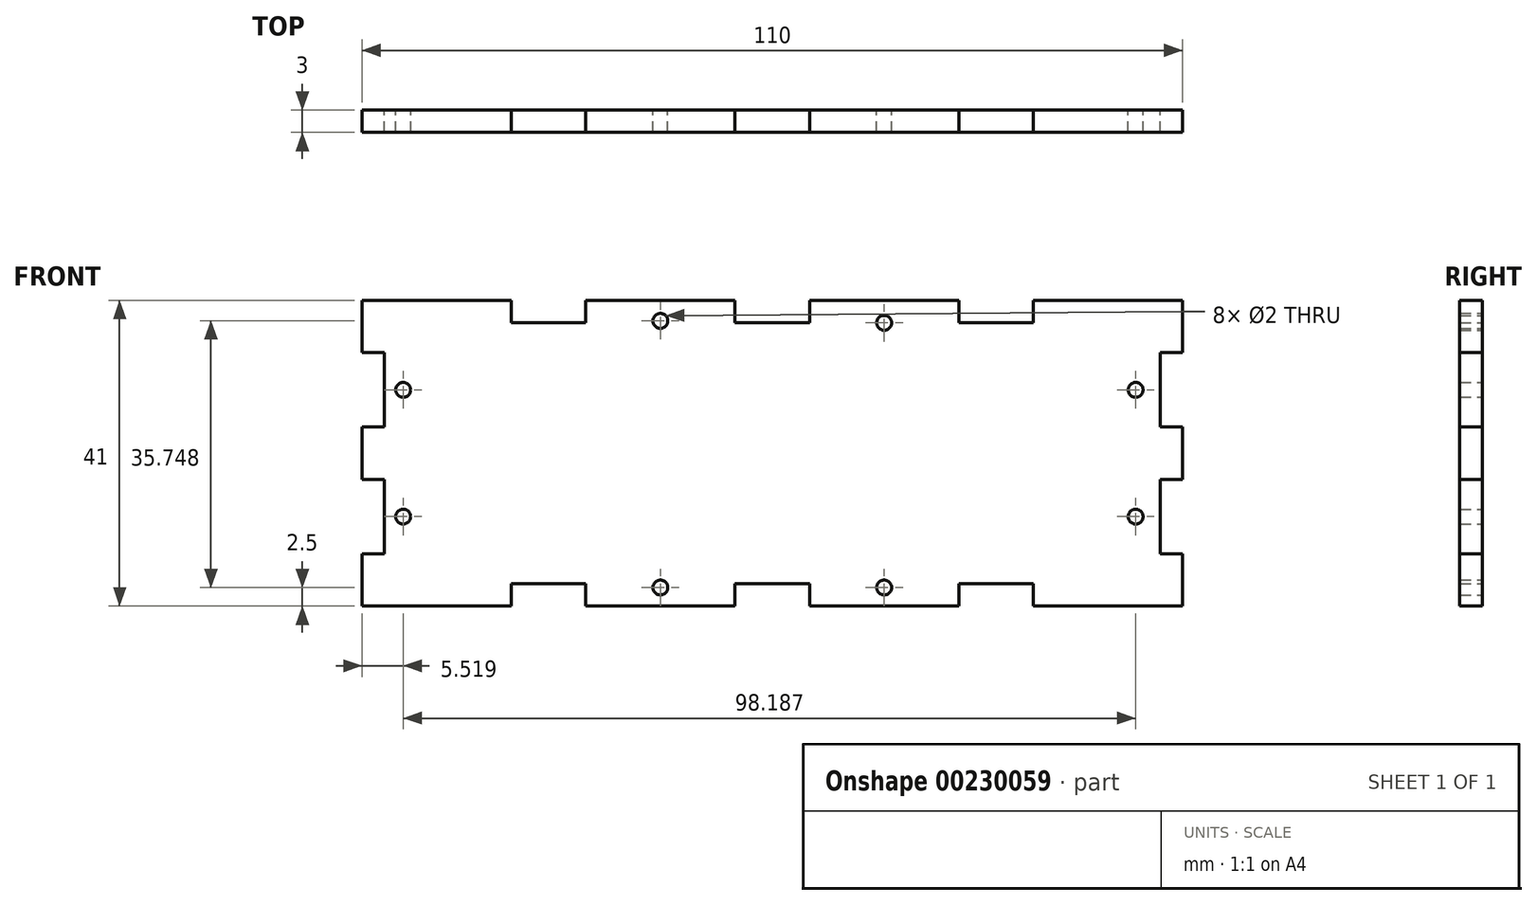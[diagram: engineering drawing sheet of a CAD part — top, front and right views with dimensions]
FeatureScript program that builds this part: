
annotation { "Feature Type Name" : "Feature", "Feature Type Description" : "" }
export const myFeature = defineFeature(function(context is Context, id is Id, definition is map)
    precondition{}
    {
        {
            var Q0;
            Q0=qCreatedBy(makeId("Front.planeOp"),FACE);
            var sketch = newSketch(context, id + "F0", { "sketchPlane" : qUnion([Q0])});
            skLineSegment(sketch, "E0", {"start": v(-54.97, 1.92) * mm, "end": v(-51.97, 1.92) * mm});
            skLineSegment(sketch, "E1", {"start": v(-51.97, 1.92) * mm, "end": v(-51.97, 11.92) * mm});
            skLineSegment(sketch, "E2", {"start": v(-51.97, 11.92) * mm, "end": v(-54.97, 11.92) * mm});
            skLineSegment(sketch, "E3", {"start": v(-54.97, 11.92) * mm, "end": v(-54.97, 18.92) * mm});
            skLineSegment(sketch, "E4", {"start": v(-54.97, 18.92) * mm, "end": v(-34.97, 18.92) * mm});
            skLineSegment(sketch, "E5", {"start": v(-34.97, 18.92) * mm, "end": v(-34.97, 15.92) * mm});
            skLineSegment(sketch, "E6", {"start": v(-34.97, 15.92) * mm, "end": v(-24.97, 15.92) * mm});
            skLineSegment(sketch, "E7", {"start": v(-24.97, 15.92) * mm, "end": v(-24.97, 18.92) * mm});
            skLineSegment(sketch, "E8", {"start": v(-4.97, 18.92) * mm, "end": v(-24.97, 18.92) * mm});
            skLineSegment(sketch, "E9", {"start": v(-4.97, 18.92) * mm, "end": v(-4.97, 15.92) * mm});
            skLineSegment(sketch, "E10", {"start": v(0.03, 15.92) * mm, "end": v(-4.97, 15.92) * mm});
            skCircle(sketch, "E11", {"center": v(-14.97, 16.17) * mm, "radius": 1 * mm});
            skCircle(sketch, "E12", {"center": v(-49.45, 6.92) * mm, "radius": 1 * mm});
            skCircle(sketch, "E13.MirrorC", {"center": v(15.03, 15.9) * mm, "radius": 1 * mm});
            skLineSegment(sketch, "E14", {"start": v(-54.97, 1.92) * mm, "end": v(-54.97, -1.58) * mm});
            skLineSegment(sketch, "E15.MirrorCS", {"start": v(52.03, 11.92) * mm, "end": v(55.03, 11.92) * mm});
            skLineSegment(sketch, "E16.MirrorCS", {"start": v(5.03, 18.92) * mm, "end": v(5.03, 15.92) * mm});
            skLineSegment(sketch, "E17.MirrorCS", {"start": v(35.03, 18.92) * mm, "end": v(35.03, 15.92) * mm});
            skLineSegment(sketch, "E18.MirrorCS", {"start": v(55.03, 1.92) * mm, "end": v(52.03, 1.92) * mm});
            skLineSegment(sketch, "E19.MirrorCS", {"start": v(25.03, 15.92) * mm, "end": v(25.03, 18.92) * mm});
            skCircle(sketch, "E20.MirrorC", {"center": v(48.74, 6.92) * mm, "radius": 1 * mm});
            skLineSegment(sketch, "E21.MirrorCS", {"start": v(55.03, 1.92) * mm, "end": v(55.03, -1.58) * mm});
            skLineSegment(sketch, "E22.MirrorCS", {"start": v(55.03, 11.92) * mm, "end": v(55.03, 18.92) * mm});
            skLineSegment(sketch, "E23.MirrorCS", {"start": v(5.03, 18.92) * mm, "end": v(25.03, 18.92) * mm});
            skLineSegment(sketch, "E24.MirrorCS", {"start": v(35.03, 15.92) * mm, "end": v(25.03, 15.92) * mm});
            skLineSegment(sketch, "E25.MirrorCS", {"start": v(52.03, 1.92) * mm, "end": v(52.03, 11.92) * mm});
            skLineSegment(sketch, "E26.MirrorCS", {"start": v(55.03, 18.92) * mm, "end": v(35.03, 18.92) * mm});
            skLineSegment(sketch, "E27", {"start": v(5.03, 15.92) * mm, "end": v(0.03, 15.92) * mm});
            skLineSegment(sketch, "E28", {"start": v(-54.97, -1.58) * mm, "end": v(55.03, -1.58) * mm, "construction": true});
            skLineSegment(sketch, "E29.MirrorCS", {"start": v(25.03, -19.08) * mm, "end": v(25.03, -22.08) * mm});
            skLineSegment(sketch, "E30.MirrorCS", {"start": v(-4.97, -22.08) * mm, "end": v(-4.97, -19.08) * mm});
            skLineSegment(sketch, "E31.MirrorCS", {"start": v(-54.97, -5.08) * mm, "end": v(-51.97, -5.08) * mm});
            skLineSegment(sketch, "E32.MirrorCS", {"start": v(-34.97, -22.08) * mm, "end": v(-34.97, -19.08) * mm});
            skLineSegment(sketch, "E33.MirrorCS", {"start": v(35.03, -22.08) * mm, "end": v(35.03, -19.08) * mm});
            skLineSegment(sketch, "E34.MirrorCS", {"start": v(-51.97, -15.08) * mm, "end": v(-54.97, -15.08) * mm});
            skLineSegment(sketch, "E35.MirrorCS", {"start": v(5.03, -22.08) * mm, "end": v(5.03, -19.08) * mm});
            skLineSegment(sketch, "E36.MirrorCS", {"start": v(55.03, -5.08) * mm, "end": v(52.03, -5.08) * mm});
            skLineSegment(sketch, "E37.MirrorCS", {"start": v(-24.97, -19.08) * mm, "end": v(-24.97, -22.08) * mm});
            skLineSegment(sketch, "E38.MirrorCS", {"start": v(52.03, -15.08) * mm, "end": v(55.03, -15.08) * mm});
            skCircle(sketch, "E39.MirrorC", {"center": v(-49.45, -10.08) * mm, "radius": 1 * mm});
            skCircle(sketch, "E40.MirrorC", {"center": v(48.74, -10.08) * mm, "radius": 1 * mm});
            skLineSegment(sketch, "E41.MirrorCS", {"start": v(-51.97, -5.08) * mm, "end": v(-51.97, -15.08) * mm});
            skLineSegment(sketch, "E42.MirrorCS", {"start": v(5.03, -19.08) * mm, "end": v(0.03, -19.08) * mm});
            skLineSegment(sketch, "E43.MirrorCS", {"start": v(35.03, -19.08) * mm, "end": v(25.03, -19.08) * mm});
            skLineSegment(sketch, "E44.MirrorCS", {"start": v(55.03, -22.08) * mm, "end": v(35.03, -22.08) * mm});
            skLineSegment(sketch, "E45.MirrorCS", {"start": v(0.03, -19.08) * mm, "end": v(-4.97, -19.08) * mm});
            skLineSegment(sketch, "E46.MirrorCS", {"start": v(-54.97, -15.08) * mm, "end": v(-54.97, -22.08) * mm});
            skLineSegment(sketch, "E47.MirrorCS", {"start": v(-34.97, -19.08) * mm, "end": v(-24.97, -19.08) * mm});
            skLineSegment(sketch, "E48.MirrorCS", {"start": v(55.03, -15.08) * mm, "end": v(55.03, -22.08) * mm});
            skLineSegment(sketch, "E49.MirrorCS", {"start": v(5.03, -22.08) * mm, "end": v(25.03, -22.08) * mm});
            skLineSegment(sketch, "E50.MirrorCS", {"start": v(52.03, -5.08) * mm, "end": v(52.03, -15.08) * mm});
            skLineSegment(sketch, "E51.MirrorCS", {"start": v(-54.97, -22.08) * mm, "end": v(-34.97, -22.08) * mm});
            skLineSegment(sketch, "E52.MirrorCS", {"start": v(-4.97, -22.08) * mm, "end": v(-24.97, -22.08) * mm});
            skLineSegment(sketch, "E53", {"start": v(-54.97, -1.58) * mm, "end": v(-54.97, -5.08) * mm});
            skLineSegment(sketch, "E54", {"start": v(55.03, -1.58) * mm, "end": v(55.03, -5.08) * mm});
            skPoint(sketch, "E55", {"position": v(52.03, 6.92) * mm});
            skPoint(sketch, "E56", {"position": v(15.03, 18.92) * mm});
            skPoint(sketch, "E57", {"position": v(-14.97, 18.92) * mm});
            skPoint(sketch, "E58", {"position": v(-51.97, 6.92) * mm});
            skLineSegment(sketch, "E59", {"start": v(-14.97, 18.92) * mm, "end": v(-14.97, -22.08) * mm, "construction": true});
            skCircle(sketch, "E60", {"center": v(-14.97, -19.58) * mm, "radius": 1 * mm});
            skLineSegment(sketch, "E61", {"start": v(15.03, 18.92) * mm, "end": v(15.03, -22.08) * mm, "construction": true});
            skCircle(sketch, "E62", {"center": v(15.03, -19.58) * mm, "radius": 1 * mm});
            skSolve(sketch);
        }
        {
            var Q0;
            Q0 = qSketchRegion(id + "F0", true);
            extrude(context, id + "F1", {"entities" : qUnion([Q0]), "depth" : 3 * mm});
        }
    });
